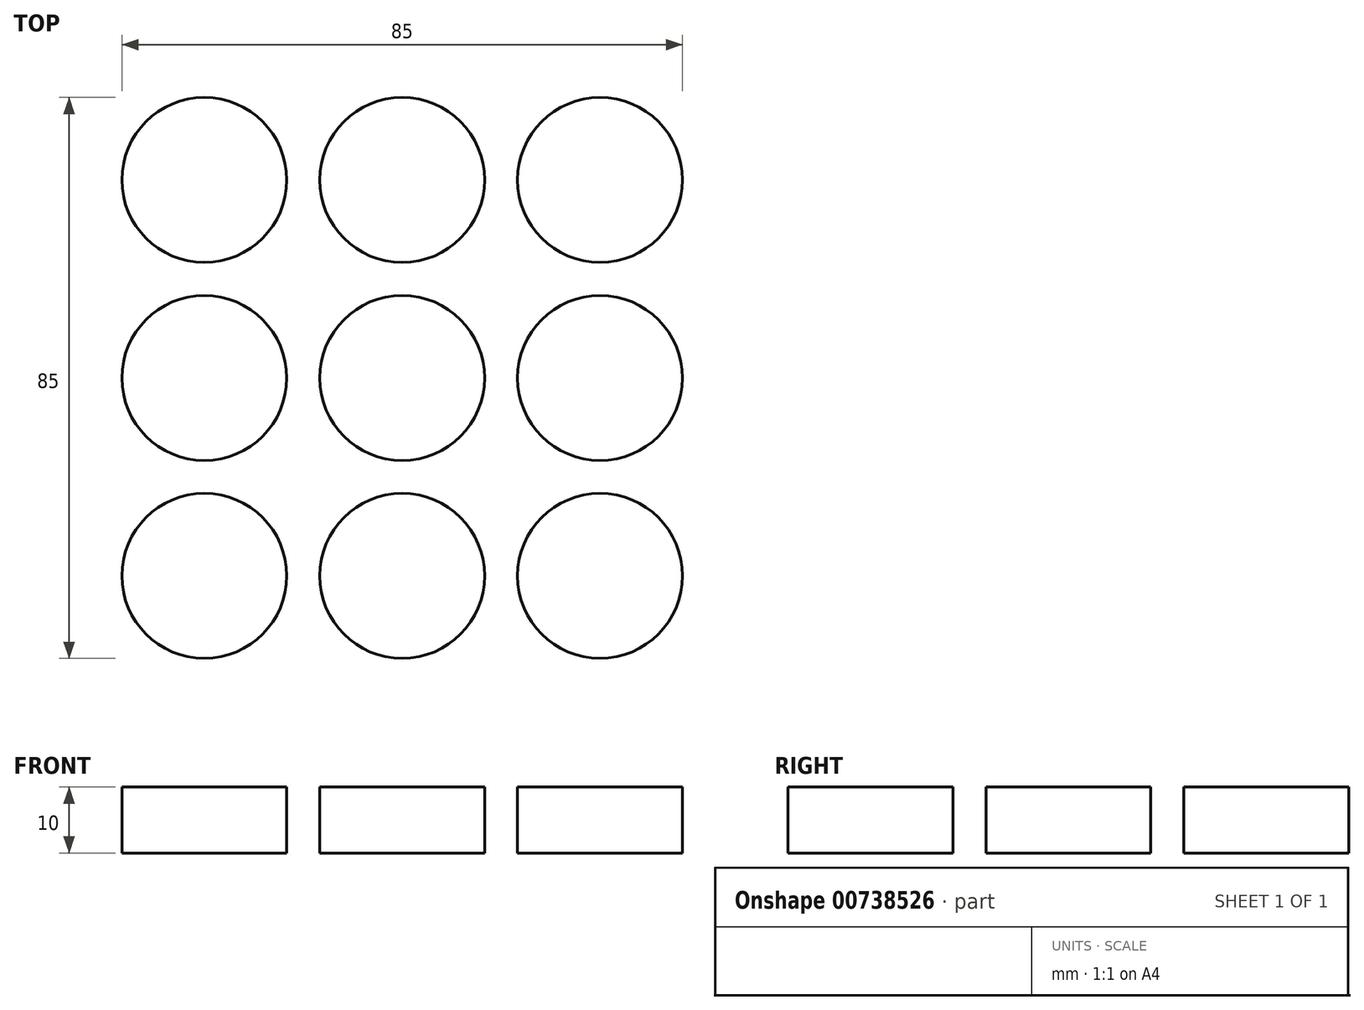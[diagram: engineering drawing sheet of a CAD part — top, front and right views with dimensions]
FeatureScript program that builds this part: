
annotation { "Feature Type Name" : "Feature", "Feature Type Description" : "" }
export const myFeature = defineFeature(function(context is Context, id is Id, definition is map)
    precondition{}
    {
        {
            var Q0;
            Q0=qCreatedBy(makeId("Top.planeOp"),FACE);
            var sketch = newSketch(context, id + "F0", { "sketchPlane" : qUnion([Q0])});
            skCircle(sketch, "E0", {"center": v(0, 0) * mm, "radius": 12.5 * mm});
            skCircle(sketch, "E1", {"center": v(0, -30) * mm, "radius": 12.5 * mm});
            skCircle(sketch, "E2", {"center": v(-30, -30) * mm, "radius": 12.5 * mm});
            skCircle(sketch, "E3", {"center": v(-30, 0) * mm, "radius": 12.5 * mm});
            skCircle(sketch, "E4", {"center": v(-30, 30) * mm, "radius": 12.5 * mm});
            skCircle(sketch, "E5", {"center": v(0, 30) * mm, "radius": 12.5 * mm});
            skCircle(sketch, "E6", {"center": v(30, 30) * mm, "radius": 12.5 * mm});
            skCircle(sketch, "E7", {"center": v(30, 0) * mm, "radius": 12.5 * mm});
            skCircle(sketch, "E8", {"center": v(30, -30) * mm, "radius": 12.5 * mm});
            skLineSegment(sketch, "E9.0", {"start": v(-47.5, 0) * mm, "end": v(-47.5, 47.5) * mm});
            skLineSegment(sketch, "E10.0", {"start": v(47.5, 47.5) * mm, "end": v(-47.5, 47.5) * mm});
            skLineSegment(sketch, "E11.0", {"start": v(47.5, -47.5) * mm, "end": v(-47.5, -47.5) * mm});
            skLineSegment(sketch, "E12.0", {"start": v(47.5, 47.5) * mm, "end": v(47.5, -47.5) * mm});
            skLineSegment(sketch, "E13.0", {"start": v(-47.5, -47.5) * mm, "end": v(-47.5, 47.5) * mm});
            skPoint(sketch, "E14.orphan", {"position": v(-62.5, 30) * mm});
            skPoint(sketch, "E15.orphan", {"position": v(0, -62.5) * mm});
            skPoint(sketch, "E16.orphan", {"position": v(-62.5, -30) * mm});
            skPoint(sketch, "E17.orphan", {"position": v(62.5, 62.5) * mm});
            skPoint(sketch, "E18.orphan", {"position": v(62.5, -62.5) * mm});
            skPoint(sketch, "E19.end.orphan", {"position": v(-62.5, -62.5) * mm});
            skPoint(sketch, "E20.0.start.orphan", {"position": v(62.5, 30) * mm});
            skPoint(sketch, "E21.orphan", {"position": v(62.5, 0) * mm});
            skPoint(sketch, "E22.0.start.orphan", {"position": v(62.5, -30) * mm});
            skSolve(sketch);
        }
        {
            var Q0;
            Q0=makeQuery(id+"F0.imprint","IMPRINT",FACE,{"disambiguationData":[TD([[makeQuery(id+"F0.imprint","IMPRINT",EDGE,{"derivedFrom":sQuery(id+"F0.wireOp",EDGE,"E2")}),1.0]])]});
            var Q1;
            Q1=makeQuery(id+"F0.imprint","IMPRINT",FACE,{"disambiguationData":[TD([[makeQuery(id+"F0.imprint","IMPRINT",EDGE,{"derivedFrom":sQuery(id+"F0.wireOp",EDGE,"E3")}),1.0]])]});
            var Q2;
            Q2=makeQuery(id+"F0.imprint","IMPRINT",FACE,{"disambiguationData":[TD([[makeQuery(id+"F0.imprint","IMPRINT",EDGE,{"derivedFrom":sQuery(id+"F0.wireOp",EDGE,"E4")}),1.0]])]});
            var Q3;
            Q3=makeQuery(id+"F0.imprint","IMPRINT",FACE,{"disambiguationData":[TD([[makeQuery(id+"F0.imprint","IMPRINT",EDGE,{"derivedFrom":sQuery(id+"F0.wireOp",EDGE,"E5")}),1.0]])]});
            var Q4;
            Q4=makeQuery(id+"F0.imprint","IMPRINT",FACE,{"disambiguationData":[TD([[makeQuery(id+"F0.imprint","IMPRINT",EDGE,{"derivedFrom":sQuery(id+"F0.wireOp",EDGE,"E0")}),1.0]])]});
            var Q5;
            Q5=makeQuery(id+"F0.imprint","IMPRINT",FACE,{"disambiguationData":[TD([[makeQuery(id+"F0.imprint","IMPRINT",EDGE,{"derivedFrom":sQuery(id+"F0.wireOp",EDGE,"E1")}),1.0]])]});
            var Q6;
            Q6=makeQuery(id+"F0.imprint","IMPRINT",FACE,{"disambiguationData":[TD([[makeQuery(id+"F0.imprint","IMPRINT",EDGE,{"derivedFrom":sQuery(id+"F0.wireOp",EDGE,"E8")}),1.0]])]});
            var Q7;
            Q7=makeQuery(id+"F0.imprint","IMPRINT",FACE,{"disambiguationData":[TD([[makeQuery(id+"F0.imprint","IMPRINT",EDGE,{"derivedFrom":sQuery(id+"F0.wireOp",EDGE,"E7")}),1.0]])]});
            var Q8;
            Q8=makeQuery(id+"F0.imprint","IMPRINT",FACE,{"disambiguationData":[TD([[makeQuery(id+"F0.imprint","IMPRINT",EDGE,{"derivedFrom":sQuery(id+"F0.wireOp",EDGE,"E6")}),1.0]])]});
            extrude(context, id + "F1", {"entities" : qUnion([Q0, Q1, Q2, Q3, Q4, Q5, Q6, Q7, Q8]), "depth" : 10 * mm, "offsetDistance" : 25 * mm});
        }
    });
